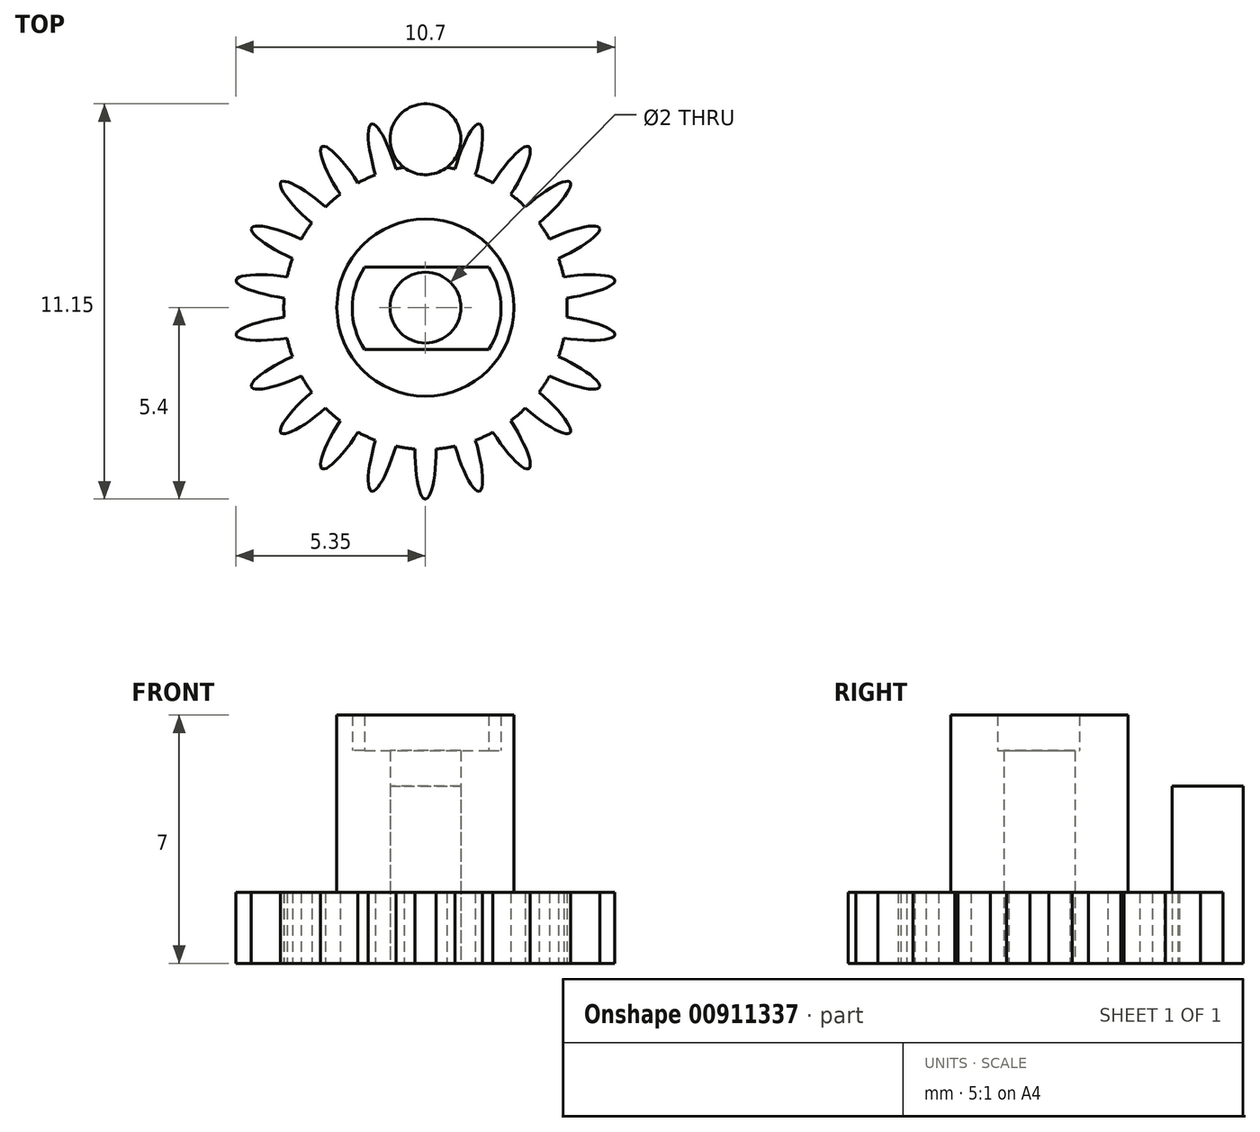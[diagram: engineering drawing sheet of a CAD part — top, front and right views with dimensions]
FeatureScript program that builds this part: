
annotation { "Feature Type Name" : "Feature", "Feature Type Description" : "" }
export const myFeature = defineFeature(function(context is Context, id is Id, definition is map)
    precondition{}
    {
        {
            var Q0;
            Q0=qCreatedBy(makeId("Top.planeOp"),FACE);
            var sketch = newSketch(context, id + "F0", { "sketchPlane" : qUnion([Q0])});
            skCircle(sketch, "E0", {"center": v(0, 0) * mm, "radius": 4 * mm});
            skEllipse(sketch, "E1", {"center": v(0, 4) * mm, "majorRadius": 1.4 * mm, "minorRadius": 0.3 * mm, "majorAxis": v(0, -1)});
            skEllipse(sketch, "E2.1.0", {"center": v(-1.13, 3.84) * mm, "majorRadius": 1.4 * mm, "minorRadius": 0.3 * mm, "majorAxis": v(0.28, -0.96)});
            skEllipse(sketch, "E2.2.0", {"center": v(-2.16, 3.37) * mm, "majorRadius": 1.4 * mm, "minorRadius": 0.3 * mm, "majorAxis": v(0.54, -0.84)});
            skEllipse(sketch, "E2.3.0", {"center": v(-3.02, 2.62) * mm, "majorRadius": 1.4 * mm, "minorRadius": 0.3 * mm, "majorAxis": v(0.76, -0.65)});
            skEllipse(sketch, "E2.4.0", {"center": v(-3.64, 1.66) * mm, "majorRadius": 1.4 * mm, "minorRadius": 0.3 * mm, "majorAxis": v(0.9, -0.42)});
            skEllipse(sketch, "E2.5.0", {"center": v(-3.96, 0.57) * mm, "majorRadius": 1.4 * mm, "minorRadius": 0.3 * mm, "majorAxis": v(0.99, -0.14)});
            skEllipse(sketch, "E2.6.0", {"center": v(-3.96, -0.57) * mm, "majorRadius": 1.4 * mm, "minorRadius": 0.3 * mm, "majorAxis": v(0.99, 0.14)});
            skEllipse(sketch, "E2.7.0", {"center": v(-3.64, -1.66) * mm, "majorRadius": 1.4 * mm, "minorRadius": 0.3 * mm, "majorAxis": v(0.9, 0.42)});
            skEllipse(sketch, "E2.8.0", {"center": v(-3.02, -2.62) * mm, "majorRadius": 1.4 * mm, "minorRadius": 0.3 * mm, "majorAxis": v(0.76, 0.65)});
            skEllipse(sketch, "E2.9.0", {"center": v(-2.16, -3.37) * mm, "majorRadius": 1.4 * mm, "minorRadius": 0.3 * mm, "majorAxis": v(0.54, 0.84)});
            skEllipse(sketch, "E2.10.0", {"center": v(-1.13, -3.84) * mm, "majorRadius": 1.4 * mm, "minorRadius": 0.3 * mm, "majorAxis": v(0.28, 0.96)});
            skEllipse(sketch, "E2.11.0", {"center": v(0, -4) * mm, "majorRadius": 1.4 * mm, "minorRadius": 0.3 * mm, "majorAxis": v(0, 1)});
            skEllipse(sketch, "E2.12.0", {"center": v(1.13, -3.84) * mm, "majorRadius": 1.4 * mm, "minorRadius": 0.3 * mm, "majorAxis": v(-0.28, 0.96)});
            skEllipse(sketch, "E2.13.0", {"center": v(2.16, -3.37) * mm, "majorRadius": 1.4 * mm, "minorRadius": 0.3 * mm, "majorAxis": v(-0.54, 0.84)});
            skEllipse(sketch, "E2.14.0", {"center": v(3.02, -2.62) * mm, "majorRadius": 1.4 * mm, "minorRadius": 0.3 * mm, "majorAxis": v(-0.76, 0.65)});
            skEllipse(sketch, "E2.15.0", {"center": v(3.64, -1.66) * mm, "majorRadius": 1.4 * mm, "minorRadius": 0.3 * mm, "majorAxis": v(-0.9, 0.42)});
            skEllipse(sketch, "E2.16.0", {"center": v(3.96, -0.57) * mm, "majorRadius": 1.4 * mm, "minorRadius": 0.3 * mm, "majorAxis": v(-0.99, 0.14)});
            skEllipse(sketch, "E2.17.0", {"center": v(3.96, 0.57) * mm, "majorRadius": 1.4 * mm, "minorRadius": 0.3 * mm, "majorAxis": v(-0.99, -0.14)});
            skEllipse(sketch, "E2.18.0", {"center": v(3.64, 1.66) * mm, "majorRadius": 1.4 * mm, "minorRadius": 0.3 * mm, "majorAxis": v(-0.9, -0.42)});
            skEllipse(sketch, "E2.19.0", {"center": v(3.02, 2.62) * mm, "majorRadius": 1.4 * mm, "minorRadius": 0.3 * mm, "majorAxis": v(-0.76, -0.65)});
            skEllipse(sketch, "E2.20.0", {"center": v(2.16, 3.37) * mm, "majorRadius": 1.4 * mm, "minorRadius": 0.3 * mm, "majorAxis": v(-0.54, -0.84)});
            skEllipse(sketch, "E2.21.0", {"center": v(1.13, 3.84) * mm, "majorRadius": 1.4 * mm, "minorRadius": 0.3 * mm, "majorAxis": v(-0.28, -0.96)});
            skCircle(sketch, "E3", {"center": v(0, 0) * mm, "radius": 2.5 * mm});
            skCircle(sketch, "E4", {"center": v(0.03, -0.02) * mm, "radius": 2.1 * mm});
            skCircle(sketch, "E5", {"center": v(0, 0) * mm, "radius": 1 * mm});
            skLineSegment(sketch, "E6", {"start": v(1.78, 1.14) * mm, "end": v(-1.72, 1.14) * mm});
            skLineSegment(sketch, "E7", {"start": v(1.78, -1.18) * mm, "end": v(-1.72, -1.18) * mm});
            skSolve(sketch);
        }
        {
            var Q0;
            Q0=qCreatedBy(makeId("Top.planeOp"),FACE);
            var sketch = newSketch(context, id + "F1", { "sketchPlane" : qUnion([Q0])});
            skCircle(sketch, "E8", {"center": v(0, 4.75) * mm, "radius": 1 * mm});
            skSolve(sketch);
        }
        {
            var Q0;
            Q0=makeQuery(id+"F0.imprint","IMPRINT",FACE,{"disambiguationData":[TD([[makeQuery(id+"F0.imprint","IMPRINT",EDGE,{"derivedFrom":sQuery(id+"F0.wireOp",EDGE,"E5")}),-1.0]])]});
            var Q1;
            {var subQ0=sQuery(id+"F0.wireOp",EDGE,"E7");Q1=makeQuery(id+"F0.imprint","IMPRINT",FACE,{"disambiguationData":[TD([[makeQuery(id+"F0.imprint","IMPRINT",EDGE,{"derivedFrom":subQ0}),1.0]])]});}
            var Q2;
            {var subQ0=sQuery(id+"F0.wireOp",EDGE,"E2.17.0");var subQ1=sQuery(id+"F0.wireOp",EDGE,"E0");var subQ2=makeQuery(id+"F0.imprint","INTERSECT",VERTEX,{"disambiguationData":[OD(0.0)],"derivedFrom":[subQ1,subQ0]});Q2=makeQuery(id+"F0.imprint","IMPRINT",FACE,{"disambiguationData":[TD([[makeQuery(id+"F0.imprint","IMPRINT",EDGE,{"disambiguationData":[TD([[subQ2,1.0]])],"derivedFrom":subQ1}),1.0]])]});}
            var Q3;
            {var subQ0=sQuery(id+"F0.wireOp",EDGE,"E2.15.0");var subQ1=sQuery(id+"F0.wireOp",EDGE,"E0");var subQ2=makeQuery(id+"F0.imprint","INTERSECT",VERTEX,{"disambiguationData":[OD(0.0)],"derivedFrom":[subQ1,subQ0]});Q3=makeQuery(id+"F0.imprint","IMPRINT",FACE,{"disambiguationData":[TD([[makeQuery(id+"F0.imprint","IMPRINT",EDGE,{"disambiguationData":[TD([[subQ2,-1.0]])],"derivedFrom":subQ1}),1.0]])]});}
            var Q4;
            {var subQ0=sQuery(id+"F0.wireOp",EDGE,"E2.19.0");var subQ1=sQuery(id+"F0.wireOp",EDGE,"E0");var subQ2=makeQuery(id+"F0.imprint","INTERSECT",VERTEX,{"disambiguationData":[OD(0.0)],"derivedFrom":[subQ1,subQ0]});Q4=makeQuery(id+"F0.imprint","IMPRINT",FACE,{"disambiguationData":[TD([[makeQuery(id+"F0.imprint","IMPRINT",EDGE,{"disambiguationData":[TD([[subQ2,-1.0]])],"derivedFrom":subQ1}),1.0]])]});}
            var Q5;
            Q5=makeQuery(id+"F0.imprint","IMPRINT",FACE,{"disambiguationData":[TD([[makeQuery(id+"F0.imprint","IMPRINT",EDGE,{"derivedFrom":sQuery(id+"F0.wireOp",EDGE,"E3")}),1.0]])]});
            var Q6;
            {var subQ0=sQuery(id+"F0.wireOp",EDGE,"E2.11.0");var subQ1=sQuery(id+"F0.wireOp",EDGE,"E0");var subQ2=makeQuery(id+"F0.imprint","INTERSECT",VERTEX,{"disambiguationData":[OD(0.0)],"derivedFrom":[subQ1,subQ0]});Q6=makeQuery(id+"F0.imprint","IMPRINT",FACE,{"disambiguationData":[TD([[makeQuery(id+"F0.imprint","IMPRINT",EDGE,{"disambiguationData":[TD([[subQ2,-1.0]])],"derivedFrom":subQ1}),-1.0]])]});}
            var Q7;
            {var subQ0=sQuery(id+"F0.wireOp",EDGE,"E2.14.0");var subQ1=sQuery(id+"F0.wireOp",EDGE,"E0");var subQ2=makeQuery(id+"F0.imprint","INTERSECT",VERTEX,{"disambiguationData":[OD(0.0)],"derivedFrom":[subQ1,subQ0]});Q7=makeQuery(id+"F0.imprint","IMPRINT",FACE,{"disambiguationData":[TD([[makeQuery(id+"F0.imprint","IMPRINT",EDGE,{"disambiguationData":[TD([[subQ2,-1.0]])],"derivedFrom":subQ1}),-1.0]])]});}
            var Q8;
            {var subQ0=sQuery(id+"F0.wireOp",EDGE,"E2.21.0");var subQ1=sQuery(id+"F0.wireOp",EDGE,"E0");var subQ2=makeQuery(id+"F0.imprint","INTERSECT",VERTEX,{"disambiguationData":[OD(0.0)],"derivedFrom":[subQ1,subQ0]});Q8=makeQuery(id+"F0.imprint","IMPRINT",FACE,{"disambiguationData":[TD([[makeQuery(id+"F0.imprint","IMPRINT",EDGE,{"disambiguationData":[TD([[subQ2,-1.0]])],"derivedFrom":subQ1}),-1.0]])]});}
            var Q9;
            Q9=makeQuery(id+"F0.imprint","IMPRINT",FACE,{"disambiguationData":[TD([[makeQuery(id+"F0.imprint","IMPRINT",EDGE,{"derivedFrom":sQuery(id+"F0.wireOp",EDGE,"E3")}),-1.0]])]});
            var Q10;
            {var subQ0=sQuery(id+"F0.wireOp",EDGE,"E2.11.0");var subQ1=sQuery(id+"F0.wireOp",EDGE,"E0");var subQ2=makeQuery(id+"F0.imprint","INTERSECT",VERTEX,{"disambiguationData":[OD(0.0)],"derivedFrom":[subQ1,subQ0]});Q10=makeQuery(id+"F0.imprint","IMPRINT",FACE,{"disambiguationData":[TD([[makeQuery(id+"F0.imprint","IMPRINT",EDGE,{"disambiguationData":[TD([[subQ2,-1.0]])],"derivedFrom":subQ1}),1.0]])]});}
            var Q11;
            {var subQ0=sQuery(id+"F0.wireOp",EDGE,"E1");var subQ1=sQuery(id+"F0.wireOp",EDGE,"E0");var subQ2=makeQuery(id+"F0.imprint","INTERSECT",VERTEX,{"disambiguationData":[OD(0.0)],"derivedFrom":[subQ1,subQ0]});Q11=makeQuery(id+"F0.imprint","IMPRINT",FACE,{"disambiguationData":[TD([[makeQuery(id+"F0.imprint","IMPRINT",EDGE,{"disambiguationData":[TD([[subQ2,-1.0]])],"derivedFrom":subQ1}),1.0]])]});}
            var Q12;
            {var subQ0=sQuery(id+"F0.wireOp",EDGE,"E2.12.0");var subQ1=sQuery(id+"F0.wireOp",EDGE,"E0");var subQ2=makeQuery(id+"F0.imprint","INTERSECT",VERTEX,{"disambiguationData":[OD(0.0)],"derivedFrom":[subQ1,subQ0]});Q12=makeQuery(id+"F0.imprint","IMPRINT",FACE,{"disambiguationData":[TD([[makeQuery(id+"F0.imprint","IMPRINT",EDGE,{"disambiguationData":[TD([[subQ2,-1.0]])],"derivedFrom":subQ1}),1.0]])]});}
            var Q13;
            {var subQ0=sQuery(id+"F0.wireOp",EDGE,"E2.18.0");var subQ1=sQuery(id+"F0.wireOp",EDGE,"E0");var subQ2=makeQuery(id+"F0.imprint","INTERSECT",VERTEX,{"disambiguationData":[OD(0.0)],"derivedFrom":[subQ1,subQ0]});Q13=makeQuery(id+"F0.imprint","IMPRINT",FACE,{"disambiguationData":[TD([[makeQuery(id+"F0.imprint","IMPRINT",EDGE,{"disambiguationData":[TD([[subQ2,-1.0]])],"derivedFrom":subQ1}),-1.0]])]});}
            var Q14;
            {var subQ0=sQuery(id+"F0.wireOp",EDGE,"E2.19.0");var subQ1=sQuery(id+"F0.wireOp",EDGE,"E0");var subQ2=makeQuery(id+"F0.imprint","INTERSECT",VERTEX,{"disambiguationData":[OD(0.0)],"derivedFrom":[subQ1,subQ0]});Q14=makeQuery(id+"F0.imprint","IMPRINT",FACE,{"disambiguationData":[TD([[makeQuery(id+"F0.imprint","IMPRINT",EDGE,{"disambiguationData":[TD([[subQ2,-1.0]])],"derivedFrom":subQ1}),-1.0]])]});}
            var Q15;
            {var subQ0=sQuery(id+"F0.wireOp",EDGE,"E2.20.0");var subQ1=sQuery(id+"F0.wireOp",EDGE,"E0");var subQ2=makeQuery(id+"F0.imprint","INTERSECT",VERTEX,{"disambiguationData":[OD(0.0)],"derivedFrom":[subQ1,subQ0]});Q15=makeQuery(id+"F0.imprint","IMPRINT",FACE,{"disambiguationData":[TD([[makeQuery(id+"F0.imprint","IMPRINT",EDGE,{"disambiguationData":[TD([[subQ2,-1.0]])],"derivedFrom":subQ1}),1.0]])]});}
            var Q16;
            {var subQ0=sQuery(id+"F0.wireOp",EDGE,"E2.17.0");var subQ1=sQuery(id+"F0.wireOp",EDGE,"E0");var subQ2=makeQuery(id+"F0.imprint","INTERSECT",VERTEX,{"disambiguationData":[OD(0.0)],"derivedFrom":[subQ1,subQ0]});Q16=makeQuery(id+"F0.imprint","IMPRINT",FACE,{"disambiguationData":[TD([[makeQuery(id+"F0.imprint","IMPRINT",EDGE,{"disambiguationData":[TD([[subQ2,1.0]])],"derivedFrom":subQ1}),-1.0]])]});}
            var Q17;
            {var subQ0=sQuery(id+"F0.wireOp",EDGE,"E2.20.0");var subQ1=sQuery(id+"F0.wireOp",EDGE,"E0");var subQ2=makeQuery(id+"F0.imprint","INTERSECT",VERTEX,{"disambiguationData":[OD(0.0)],"derivedFrom":[subQ1,subQ0]});Q17=makeQuery(id+"F0.imprint","IMPRINT",FACE,{"disambiguationData":[TD([[makeQuery(id+"F0.imprint","IMPRINT",EDGE,{"disambiguationData":[TD([[subQ2,-1.0]])],"derivedFrom":subQ1}),-1.0]])]});}
            var Q18;
            {var subQ0=sQuery(id+"F0.wireOp",EDGE,"E2.18.0");var subQ1=sQuery(id+"F0.wireOp",EDGE,"E0");var subQ2=makeQuery(id+"F0.imprint","INTERSECT",VERTEX,{"disambiguationData":[OD(0.0)],"derivedFrom":[subQ1,subQ0]});Q18=makeQuery(id+"F0.imprint","IMPRINT",FACE,{"disambiguationData":[TD([[makeQuery(id+"F0.imprint","IMPRINT",EDGE,{"disambiguationData":[TD([[subQ2,-1.0]])],"derivedFrom":subQ1}),1.0]])]});}
            var Q19;
            {var subQ0=sQuery(id+"F0.wireOp",EDGE,"E2.12.0");var subQ1=sQuery(id+"F0.wireOp",EDGE,"E0");var subQ2=makeQuery(id+"F0.imprint","INTERSECT",VERTEX,{"disambiguationData":[OD(0.0)],"derivedFrom":[subQ1,subQ0]});Q19=makeQuery(id+"F0.imprint","IMPRINT",FACE,{"disambiguationData":[TD([[makeQuery(id+"F0.imprint","IMPRINT",EDGE,{"disambiguationData":[TD([[subQ2,-1.0]])],"derivedFrom":subQ1}),-1.0]])]});}
            var Q20;
            {var subQ0=sQuery(id+"F0.wireOp",EDGE,"E1");var subQ1=sQuery(id+"F0.wireOp",EDGE,"E0");var subQ2=makeQuery(id+"F0.imprint","INTERSECT",VERTEX,{"disambiguationData":[OD(0.0)],"derivedFrom":[subQ1,subQ0]});Q20=makeQuery(id+"F0.imprint","IMPRINT",FACE,{"disambiguationData":[TD([[makeQuery(id+"F0.imprint","IMPRINT",EDGE,{"disambiguationData":[TD([[subQ2,-1.0]])],"derivedFrom":subQ1}),-1.0]])]});}
            var Q21;
            {var subQ0=sQuery(id+"F0.wireOp",EDGE,"E2.15.0");var subQ1=sQuery(id+"F0.wireOp",EDGE,"E0");var subQ2=makeQuery(id+"F0.imprint","INTERSECT",VERTEX,{"disambiguationData":[OD(0.0)],"derivedFrom":[subQ1,subQ0]});Q21=makeQuery(id+"F0.imprint","IMPRINT",FACE,{"disambiguationData":[TD([[makeQuery(id+"F0.imprint","IMPRINT",EDGE,{"disambiguationData":[TD([[subQ2,-1.0]])],"derivedFrom":subQ1}),-1.0]])]});}
            var Q22;
            {var subQ0=sQuery(id+"F0.wireOp",EDGE,"E2.14.0");var subQ1=sQuery(id+"F0.wireOp",EDGE,"E0");var subQ2=makeQuery(id+"F0.imprint","INTERSECT",VERTEX,{"disambiguationData":[OD(0.0)],"derivedFrom":[subQ1,subQ0]});Q22=makeQuery(id+"F0.imprint","IMPRINT",FACE,{"disambiguationData":[TD([[makeQuery(id+"F0.imprint","IMPRINT",EDGE,{"disambiguationData":[TD([[subQ2,-1.0]])],"derivedFrom":subQ1}),1.0]])]});}
            var Q23;
            {var subQ0=sQuery(id+"F0.wireOp",EDGE,"E2.13.0");var subQ1=sQuery(id+"F0.wireOp",EDGE,"E0");var subQ2=makeQuery(id+"F0.imprint","INTERSECT",VERTEX,{"disambiguationData":[OD(0.0)],"derivedFrom":[subQ1,subQ0]});Q23=makeQuery(id+"F0.imprint","IMPRINT",FACE,{"disambiguationData":[TD([[makeQuery(id+"F0.imprint","IMPRINT",EDGE,{"disambiguationData":[TD([[subQ2,-1.0]])],"derivedFrom":subQ1}),-1.0]])]});}
            var Q24;
            {var subQ0=sQuery(id+"F0.wireOp",EDGE,"E2.13.0");var subQ1=sQuery(id+"F0.wireOp",EDGE,"E0");var subQ2=makeQuery(id+"F0.imprint","INTERSECT",VERTEX,{"disambiguationData":[OD(0.0)],"derivedFrom":[subQ1,subQ0]});Q24=makeQuery(id+"F0.imprint","IMPRINT",FACE,{"disambiguationData":[TD([[makeQuery(id+"F0.imprint","IMPRINT",EDGE,{"disambiguationData":[TD([[subQ2,-1.0]])],"derivedFrom":subQ1}),1.0]])]});}
            var Q25;
            {var subQ0=sQuery(id+"F0.wireOp",EDGE,"E2.21.0");var subQ1=sQuery(id+"F0.wireOp",EDGE,"E0");var subQ2=makeQuery(id+"F0.imprint","INTERSECT",VERTEX,{"disambiguationData":[OD(0.0)],"derivedFrom":[subQ1,subQ0]});Q25=makeQuery(id+"F0.imprint","IMPRINT",FACE,{"disambiguationData":[TD([[makeQuery(id+"F0.imprint","IMPRINT",EDGE,{"disambiguationData":[TD([[subQ2,-1.0]])],"derivedFrom":subQ1}),1.0]])]});}
            var Q26;
            {var subQ0=sQuery(id+"F0.wireOp",EDGE,"E6");Q26=makeQuery(id+"F0.imprint","IMPRINT",FACE,{"disambiguationData":[TD([[makeQuery(id+"F0.imprint","IMPRINT",EDGE,{"derivedFrom":subQ0}),-1.0]])]});}
            var Q27;
            {var subQ0=sQuery(id+"F0.wireOp",EDGE,"E2.16.0");var subQ1=sQuery(id+"F0.wireOp",EDGE,"E0");var subQ2=makeQuery(id+"F0.imprint","INTERSECT",VERTEX,{"disambiguationData":[OD(0.0)],"derivedFrom":[subQ1,subQ0]});Q27=makeQuery(id+"F0.imprint","IMPRINT",FACE,{"disambiguationData":[TD([[makeQuery(id+"F0.imprint","IMPRINT",EDGE,{"disambiguationData":[TD([[subQ2,-1.0]])],"derivedFrom":subQ1}),1.0]])]});}
            var Q28;
            {var subQ0=sQuery(id+"F0.wireOp",EDGE,"E2.1.0");var subQ1=sQuery(id+"F0.wireOp",EDGE,"E0");var subQ2=makeQuery(id+"F0.imprint","INTERSECT",VERTEX,{"disambiguationData":[OD(0.0)],"derivedFrom":[subQ1,subQ0]});Q28=makeQuery(id+"F0.imprint","IMPRINT",FACE,{"disambiguationData":[TD([[makeQuery(id+"F0.imprint","IMPRINT",EDGE,{"disambiguationData":[TD([[subQ2,-1.0]])],"derivedFrom":subQ1}),1.0]])]});}
            var Q29;
            {var subQ0=sQuery(id+"F0.wireOp",EDGE,"E2.5.0");var subQ1=sQuery(id+"F0.wireOp",EDGE,"E0");var subQ2=makeQuery(id+"F0.imprint","INTERSECT",VERTEX,{"disambiguationData":[OD(0.0)],"derivedFrom":[subQ1,subQ0]});Q29=makeQuery(id+"F0.imprint","IMPRINT",FACE,{"disambiguationData":[TD([[makeQuery(id+"F0.imprint","IMPRINT",EDGE,{"disambiguationData":[TD([[subQ2,-1.0]])],"derivedFrom":subQ1}),1.0]])]});}
            var Q30;
            {var subQ0=sQuery(id+"F0.wireOp",EDGE,"E2.2.0");var subQ1=sQuery(id+"F0.wireOp",EDGE,"E0");var subQ2=makeQuery(id+"F0.imprint","INTERSECT",VERTEX,{"disambiguationData":[OD(0.0)],"derivedFrom":[subQ1,subQ0]});Q30=makeQuery(id+"F0.imprint","IMPRINT",FACE,{"disambiguationData":[TD([[makeQuery(id+"F0.imprint","IMPRINT",EDGE,{"disambiguationData":[TD([[subQ2,-1.0]])],"derivedFrom":subQ1}),1.0]])]});}
            var Q31;
            {var subQ0=sQuery(id+"F0.wireOp",EDGE,"E2.9.0");var subQ1=sQuery(id+"F0.wireOp",EDGE,"E0");var subQ2=makeQuery(id+"F0.imprint","INTERSECT",VERTEX,{"disambiguationData":[OD(0.0)],"derivedFrom":[subQ1,subQ0]});Q31=makeQuery(id+"F0.imprint","IMPRINT",FACE,{"disambiguationData":[TD([[makeQuery(id+"F0.imprint","IMPRINT",EDGE,{"disambiguationData":[TD([[subQ2,-1.0]])],"derivedFrom":subQ1}),-1.0]])]});}
            var Q32;
            {var subQ0=sQuery(id+"F0.wireOp",EDGE,"E2.9.0");var subQ1=sQuery(id+"F0.wireOp",EDGE,"E0");var subQ2=makeQuery(id+"F0.imprint","INTERSECT",VERTEX,{"disambiguationData":[OD(0.0)],"derivedFrom":[subQ1,subQ0]});Q32=makeQuery(id+"F0.imprint","IMPRINT",FACE,{"disambiguationData":[TD([[makeQuery(id+"F0.imprint","IMPRINT",EDGE,{"disambiguationData":[TD([[subQ2,-1.0]])],"derivedFrom":subQ1}),1.0]])]});}
            var Q33;
            {var subQ0=sQuery(id+"F0.wireOp",EDGE,"E2.3.0");var subQ1=sQuery(id+"F0.wireOp",EDGE,"E0");var subQ2=makeQuery(id+"F0.imprint","INTERSECT",VERTEX,{"disambiguationData":[OD(0.0)],"derivedFrom":[subQ1,subQ0]});Q33=makeQuery(id+"F0.imprint","IMPRINT",FACE,{"disambiguationData":[TD([[makeQuery(id+"F0.imprint","IMPRINT",EDGE,{"disambiguationData":[TD([[subQ2,-1.0]])],"derivedFrom":subQ1}),-1.0]])]});}
            var Q34;
            {var subQ0=sQuery(id+"F0.wireOp",EDGE,"E2.16.0");var subQ1=sQuery(id+"F0.wireOp",EDGE,"E0");var subQ2=makeQuery(id+"F0.imprint","INTERSECT",VERTEX,{"disambiguationData":[OD(0.0)],"derivedFrom":[subQ1,subQ0]});Q34=makeQuery(id+"F0.imprint","IMPRINT",FACE,{"disambiguationData":[TD([[makeQuery(id+"F0.imprint","IMPRINT",EDGE,{"disambiguationData":[TD([[subQ2,-1.0]])],"derivedFrom":subQ1}),-1.0]])]});}
            var Q35;
            {var subQ0=sQuery(id+"F0.wireOp",EDGE,"E2.4.0");var subQ1=sQuery(id+"F0.wireOp",EDGE,"E0");var subQ2=makeQuery(id+"F0.imprint","INTERSECT",VERTEX,{"disambiguationData":[OD(0.0)],"derivedFrom":[subQ1,subQ0]});Q35=makeQuery(id+"F0.imprint","IMPRINT",FACE,{"disambiguationData":[TD([[makeQuery(id+"F0.imprint","IMPRINT",EDGE,{"disambiguationData":[TD([[subQ2,-1.0]])],"derivedFrom":subQ1}),1.0]])]});}
            var Q36;
            {var subQ0=sQuery(id+"F0.wireOp",EDGE,"E2.7.0");var subQ1=sQuery(id+"F0.wireOp",EDGE,"E0");var subQ2=makeQuery(id+"F0.imprint","INTERSECT",VERTEX,{"disambiguationData":[OD(0.0)],"derivedFrom":[subQ1,subQ0]});Q36=makeQuery(id+"F0.imprint","IMPRINT",FACE,{"disambiguationData":[TD([[makeQuery(id+"F0.imprint","IMPRINT",EDGE,{"disambiguationData":[TD([[subQ2,-1.0]])],"derivedFrom":subQ1}),1.0]])]});}
            var Q37;
            {var subQ0=sQuery(id+"F0.wireOp",EDGE,"E2.10.0");var subQ1=sQuery(id+"F0.wireOp",EDGE,"E0");var subQ2=makeQuery(id+"F0.imprint","INTERSECT",VERTEX,{"disambiguationData":[OD(0.0)],"derivedFrom":[subQ1,subQ0]});Q37=makeQuery(id+"F0.imprint","IMPRINT",FACE,{"disambiguationData":[TD([[makeQuery(id+"F0.imprint","IMPRINT",EDGE,{"disambiguationData":[TD([[subQ2,-1.0]])],"derivedFrom":subQ1}),-1.0]])]});}
            var Q38;
            {var subQ0=sQuery(id+"F0.wireOp",EDGE,"E2.1.0");var subQ1=sQuery(id+"F0.wireOp",EDGE,"E0");var subQ2=makeQuery(id+"F0.imprint","INTERSECT",VERTEX,{"disambiguationData":[OD(0.0)],"derivedFrom":[subQ1,subQ0]});Q38=makeQuery(id+"F0.imprint","IMPRINT",FACE,{"disambiguationData":[TD([[makeQuery(id+"F0.imprint","IMPRINT",EDGE,{"disambiguationData":[TD([[subQ2,-1.0]])],"derivedFrom":subQ1}),-1.0]])]});}
            var Q39;
            {var subQ0=sQuery(id+"F0.wireOp",EDGE,"E2.5.0");var subQ1=sQuery(id+"F0.wireOp",EDGE,"E0");var subQ2=makeQuery(id+"F0.imprint","INTERSECT",VERTEX,{"disambiguationData":[OD(0.0)],"derivedFrom":[subQ1,subQ0]});Q39=makeQuery(id+"F0.imprint","IMPRINT",FACE,{"disambiguationData":[TD([[makeQuery(id+"F0.imprint","IMPRINT",EDGE,{"disambiguationData":[TD([[subQ2,-1.0]])],"derivedFrom":subQ1}),-1.0]])]});}
            var Q40;
            {var subQ0=sQuery(id+"F0.wireOp",EDGE,"E2.8.0");var subQ1=sQuery(id+"F0.wireOp",EDGE,"E0");var subQ2=makeQuery(id+"F0.imprint","INTERSECT",VERTEX,{"disambiguationData":[OD(0.0)],"derivedFrom":[subQ1,subQ0]});Q40=makeQuery(id+"F0.imprint","IMPRINT",FACE,{"disambiguationData":[TD([[makeQuery(id+"F0.imprint","IMPRINT",EDGE,{"disambiguationData":[TD([[subQ2,-1.0]])],"derivedFrom":subQ1}),1.0]])]});}
            var Q41;
            {var subQ0=sQuery(id+"F0.wireOp",EDGE,"E2.2.0");var subQ1=sQuery(id+"F0.wireOp",EDGE,"E0");var subQ2=makeQuery(id+"F0.imprint","INTERSECT",VERTEX,{"disambiguationData":[OD(0.0)],"derivedFrom":[subQ1,subQ0]});Q41=makeQuery(id+"F0.imprint","IMPRINT",FACE,{"disambiguationData":[TD([[makeQuery(id+"F0.imprint","IMPRINT",EDGE,{"disambiguationData":[TD([[subQ2,-1.0]])],"derivedFrom":subQ1}),-1.0]])]});}
            var Q42;
            {var subQ0=sQuery(id+"F0.wireOp",EDGE,"E2.4.0");var subQ1=sQuery(id+"F0.wireOp",EDGE,"E0");var subQ2=makeQuery(id+"F0.imprint","INTERSECT",VERTEX,{"disambiguationData":[OD(0.0)],"derivedFrom":[subQ1,subQ0]});Q42=makeQuery(id+"F0.imprint","IMPRINT",FACE,{"disambiguationData":[TD([[makeQuery(id+"F0.imprint","IMPRINT",EDGE,{"disambiguationData":[TD([[subQ2,-1.0]])],"derivedFrom":subQ1}),-1.0]])]});}
            var Q43;
            {var subQ0=sQuery(id+"F0.wireOp",EDGE,"E2.10.0");var subQ1=sQuery(id+"F0.wireOp",EDGE,"E0");var subQ2=makeQuery(id+"F0.imprint","INTERSECT",VERTEX,{"disambiguationData":[OD(0.0)],"derivedFrom":[subQ1,subQ0]});Q43=makeQuery(id+"F0.imprint","IMPRINT",FACE,{"disambiguationData":[TD([[makeQuery(id+"F0.imprint","IMPRINT",EDGE,{"disambiguationData":[TD([[subQ2,-1.0]])],"derivedFrom":subQ1}),1.0]])]});}
            var Q44;
            {var subQ0=sQuery(id+"F0.wireOp",EDGE,"E2.6.0");var subQ1=sQuery(id+"F0.wireOp",EDGE,"E0");var subQ2=makeQuery(id+"F0.imprint","INTERSECT",VERTEX,{"disambiguationData":[OD(0.0)],"derivedFrom":[subQ1,subQ0]});Q44=makeQuery(id+"F0.imprint","IMPRINT",FACE,{"disambiguationData":[TD([[makeQuery(id+"F0.imprint","IMPRINT",EDGE,{"disambiguationData":[TD([[subQ2,-1.0]])],"derivedFrom":subQ1}),-1.0]])]});}
            var Q45;
            {var subQ0=sQuery(id+"F0.wireOp",EDGE,"E2.6.0");var subQ1=sQuery(id+"F0.wireOp",EDGE,"E0");var subQ2=makeQuery(id+"F0.imprint","INTERSECT",VERTEX,{"disambiguationData":[OD(0.0)],"derivedFrom":[subQ1,subQ0]});Q45=makeQuery(id+"F0.imprint","IMPRINT",FACE,{"disambiguationData":[TD([[makeQuery(id+"F0.imprint","IMPRINT",EDGE,{"disambiguationData":[TD([[subQ2,-1.0]])],"derivedFrom":subQ1}),1.0]])]});}
            var Q46;
            {var subQ0=sQuery(id+"F0.wireOp",EDGE,"E2.3.0");var subQ1=sQuery(id+"F0.wireOp",EDGE,"E0");var subQ2=makeQuery(id+"F0.imprint","INTERSECT",VERTEX,{"disambiguationData":[OD(0.0)],"derivedFrom":[subQ1,subQ0]});Q46=makeQuery(id+"F0.imprint","IMPRINT",FACE,{"disambiguationData":[TD([[makeQuery(id+"F0.imprint","IMPRINT",EDGE,{"disambiguationData":[TD([[subQ2,-1.0]])],"derivedFrom":subQ1}),1.0]])]});}
            var Q47;
            {var subQ0=sQuery(id+"F0.wireOp",EDGE,"E2.8.0");var subQ1=sQuery(id+"F0.wireOp",EDGE,"E0");var subQ2=makeQuery(id+"F0.imprint","INTERSECT",VERTEX,{"disambiguationData":[OD(0.0)],"derivedFrom":[subQ1,subQ0]});Q47=makeQuery(id+"F0.imprint","IMPRINT",FACE,{"disambiguationData":[TD([[makeQuery(id+"F0.imprint","IMPRINT",EDGE,{"disambiguationData":[TD([[subQ2,-1.0]])],"derivedFrom":subQ1}),-1.0]])]});}
            var Q48;
            {var subQ0=sQuery(id+"F0.wireOp",EDGE,"E2.7.0");var subQ1=sQuery(id+"F0.wireOp",EDGE,"E0");var subQ2=makeQuery(id+"F0.imprint","INTERSECT",VERTEX,{"disambiguationData":[OD(0.0)],"derivedFrom":[subQ1,subQ0]});Q48=makeQuery(id+"F0.imprint","IMPRINT",FACE,{"disambiguationData":[TD([[makeQuery(id+"F0.imprint","IMPRINT",EDGE,{"disambiguationData":[TD([[subQ2,-1.0]])],"derivedFrom":subQ1}),-1.0]])]});}
            extrude(context, id + "F2", {"entities" : qUnion([Q0, Q1, Q2, Q3, Q4, Q5, Q6, Q7, Q8, Q9, Q10, Q11, Q12, Q13, Q14, Q15, Q16, Q17, Q18, Q19, Q20, Q21, Q22, Q23, Q24, Q25, Q26, Q27, Q28, Q29, Q30, Q31, Q32, Q33, Q34, Q35, Q36, Q37, Q38, Q39, Q40, Q41, Q42, Q43, Q44, Q45, Q46, Q47, Q48]), "depth" : 2 * mm, "offsetDistance" : 25 * mm});
        }
        {
            var Q0;
            Q0=makeQuery(id+"F1.imprint","IMPRINT",FACE,{"disambiguationData":[TD([[makeQuery(id+"F1.imprint","IMPRINT",EDGE,{"derivedFrom":sQuery(id+"F1.wireOp",EDGE,"E8")}),1.0]])]});
            extrude(context, id + "F3", {"entities" : qUnion([Q0]), "operationType" : NewBodyOperationType.ADD, "depth" : 5 * mm, "offsetDistance" : 25 * mm});
        }
        {
            var Q0;
            Q0=makeQuery(id+"F0.imprint","IMPRINT",FACE,{"disambiguationData":[TD([[makeQuery(id+"F0.imprint","IMPRINT",EDGE,{"derivedFrom":sQuery(id+"F0.wireOp",EDGE,"E3")}),1.0]])]});
            var Q1;
            {var subQ0=sQuery(id+"F0.wireOp",EDGE,"E7");Q1=makeQuery(id+"F0.imprint","IMPRINT",FACE,{"disambiguationData":[TD([[makeQuery(id+"F0.imprint","IMPRINT",EDGE,{"derivedFrom":subQ0}),1.0]])]});}
            var Q2;
            {var subQ0=sQuery(id+"F0.wireOp",EDGE,"E6");Q2=makeQuery(id+"F0.imprint","IMPRINT",FACE,{"disambiguationData":[TD([[makeQuery(id+"F0.imprint","IMPRINT",EDGE,{"derivedFrom":subQ0}),-1.0]])]});}
            var Q3;
            Q3=makeQuery(id+"F0.imprint","IMPRINT",FACE,{"disambiguationData":[TD([[makeQuery(id+"F0.imprint","IMPRINT",EDGE,{"derivedFrom":sQuery(id+"F0.wireOp",EDGE,"E5")}),-1.0]])]});
            extrude(context, id + "F4", {"entities" : qUnion([Q0, Q1, Q2, Q3]), "operationType" : NewBodyOperationType.ADD, "depth" : 6 * mm, "offsetDistance" : 25 * mm});
        }
        {
            var Q0;
            Q0=makeQuery(id+"F0.imprint","IMPRINT",FACE,{"disambiguationData":[TD([[makeQuery(id+"F0.imprint","IMPRINT",EDGE,{"derivedFrom":sQuery(id+"F0.wireOp",EDGE,"E3")}),1.0]])]});
            var Q1;
            {var subQ0=sQuery(id+"F0.wireOp",EDGE,"E7");Q1=makeQuery(id+"F0.imprint","IMPRINT",FACE,{"disambiguationData":[TD([[makeQuery(id+"F0.imprint","IMPRINT",EDGE,{"derivedFrom":subQ0}),1.0]])]});}
            var Q2;
            {var subQ0=sQuery(id+"F0.wireOp",EDGE,"E6");Q2=makeQuery(id+"F0.imprint","IMPRINT",FACE,{"disambiguationData":[TD([[makeQuery(id+"F0.imprint","IMPRINT",EDGE,{"derivedFrom":subQ0}),-1.0]])]});}
            extrude(context, id + "F5", {"entities" : qUnion([Q0, Q1, Q2]), "operationType" : NewBodyOperationType.ADD, "depth" : 7 * mm, "offsetDistance" : 25 * mm});
        }
    });
